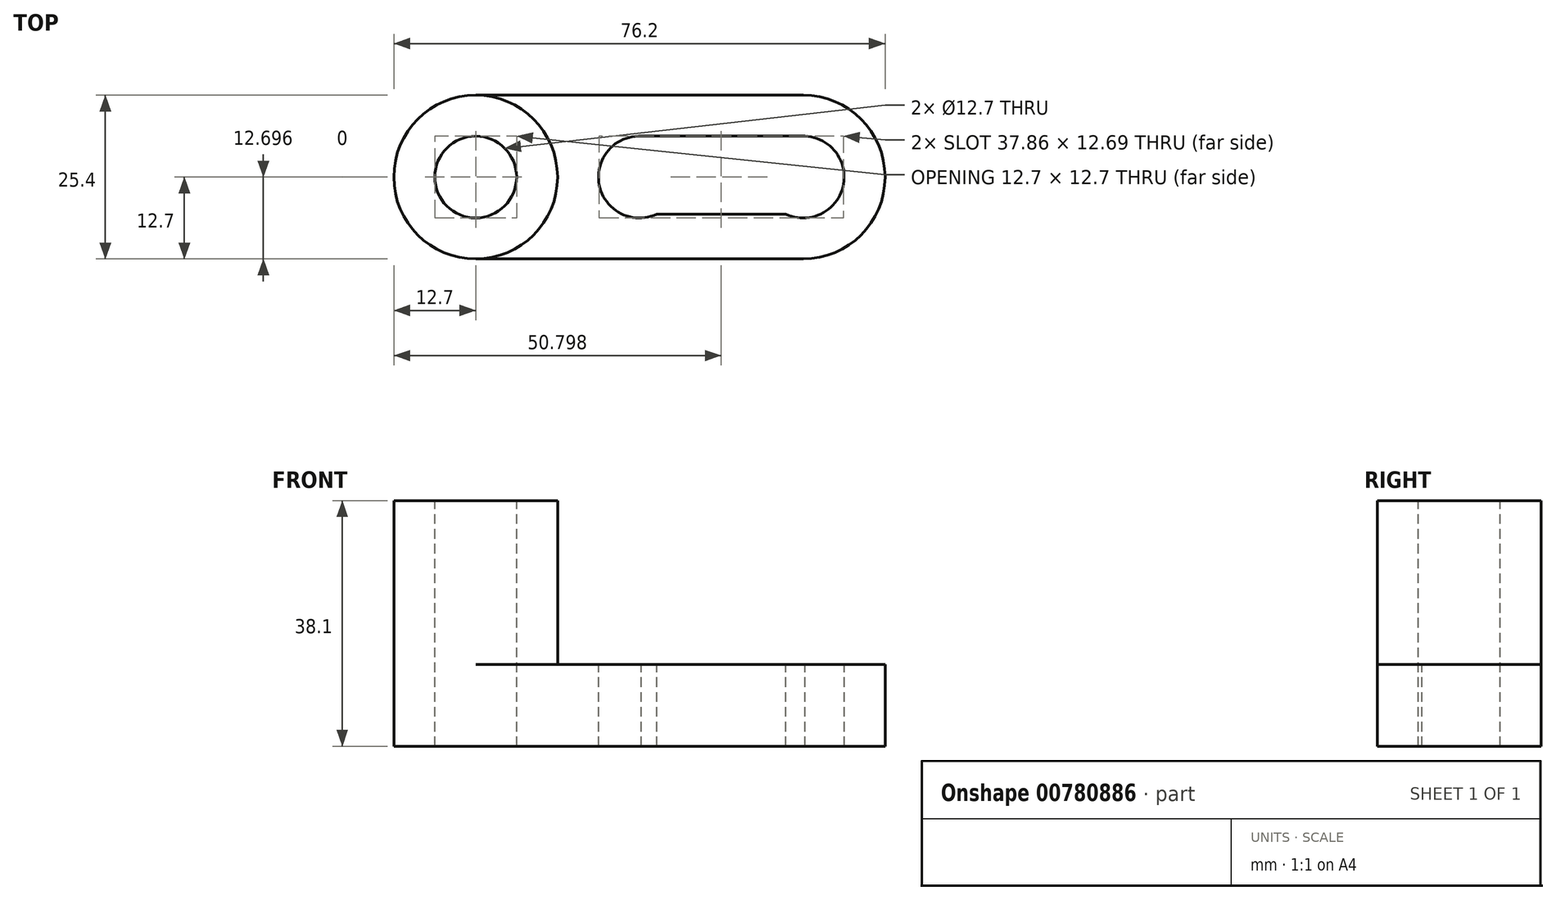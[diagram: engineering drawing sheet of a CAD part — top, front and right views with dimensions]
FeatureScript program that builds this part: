
annotation { "Feature Type Name" : "Feature", "Feature Type Description" : "" }
export const myFeature = defineFeature(function(context is Context, id is Id, definition is map)
    precondition{}
    {
        {
            var Q0;
            Q0=qCreatedBy(makeId("Front.planeOp"),FACE);
            var sketch = newSketch(context, id + "F0", { "sketchPlane" : qUnion([Q0])});
            skLineSegment(sketch, "E0", {"start": v(0, 0) * mm, "end": v(0, 38.1) * mm});
            skLineSegment(sketch, "E1", {"start": v(0, 38.1) * mm, "end": v(25.4, 38.1) * mm});
            skLineSegment(sketch, "E2", {"start": v(25.4, 38.1) * mm, "end": v(25.4, 12.7) * mm});
            skLineSegment(sketch, "E3", {"start": v(25.4, 12.7) * mm, "end": v(76.2, 12.7) * mm});
            skLineSegment(sketch, "E4", {"start": v(76.2, 12.7) * mm, "end": v(76.2, 0) * mm});
            skLineSegment(sketch, "E5", {"start": v(76.2, 0) * mm, "end": v(0, 0) * mm});
            skSolve(sketch);
        }
        {
            var Q0;
            Q0 = qSketchRegion(id + "F0", true);
            extrude(context, id + "F1", {"entities" : qUnion([Q0]), "depth" : 25.4 * mm, "offsetDistance" : 25.4 * mm});
        }
        {
            var Q0;
            Q0=makeQuery(id+"F1.opExtrude","CAP_EDGE",EDGE,{"disambiguationData":[OSD([sQuery(id+"F0.wireOp",EDGE,"E2")])],"isStart":true});
            var Q1;
            Q1=makeQuery(id+"F1.opExtrude","CAP_EDGE",EDGE,{"disambiguationData":[OSD([sQuery(id+"F0.wireOp",EDGE,"E2")])],"isStart":false});
            var Q2;
            Q2=makeQuery(id+"F1.opExtrude","CAP_EDGE",EDGE,{"disambiguationData":[OSD([sQuery(id+"F0.wireOp",EDGE,"E0")])],"isStart":false});
            var Q3;
            Q3=makeQuery(id+"F1.opExtrude","CAP_EDGE",EDGE,{"disambiguationData":[OSD([sQuery(id+"F0.wireOp",EDGE,"E0")])],"isStart":true});
            fillet(context, id + "F2", {"entities" : qUnion([Q0, Q1, Q2, Q3]), "radius" : 12.7 * mm, "tangentPropagation" : true, "allowEdgeOverflow" : false});
        }
        {
            var Q0;
            Q0=makeQuery(id+"F1.opExtrude","SWEPT_FACE",FACE,{"disambiguationData":[OSD([sQuery(id+"F0.wireOp",EDGE,"E1")])]});
            var sketch = newSketch(context, id + "F3", { "sketchPlane" : qUnion([Q0])});
            skCircle(sketch, "E6", {"center": v(12.7, -12.7) * mm, "radius": 6.35 * mm});
            skSolve(sketch);
        }
        {
            var Q0;
            Q0=makeQuery(id+"F3.imprint","IMPRINT",FACE,{"disambiguationData":[TD([[makeQuery(id+"F3.imprint","IMPRINT",EDGE,{"derivedFrom":sQuery(id+"F3.wireOp",EDGE,"E6")}),1.0]])]});
            extrude(context, id + "F4", {"entities" : qUnion([Q0]), "operationType" : NewBodyOperationType.REMOVE, "oppositeDirection" : true, "depth" : 50.8 * mm, "offsetDistance" : 25.4 * mm});
        }
        {
            var Q0;
            Q0=makeQuery(id+"F1.opExtrude","CAP_EDGE",EDGE,{"disambiguationData":[OSD([sQuery(id+"F0.wireOp",EDGE,"E4")])],"isStart":true});
            var Q1;
            Q1=makeQuery(id+"F1.opExtrude","CAP_EDGE",EDGE,{"disambiguationData":[OSD([sQuery(id+"F0.wireOp",EDGE,"E4")])],"isStart":false});
            fillet(context, id + "F5", {"entities" : qUnion([Q0, Q1]), "radius" : 12.7 * mm, "tangentPropagation" : true, "allowEdgeOverflow" : false});
        }
        {
            var Q0;
            Q0=makeQuery(id+"F1.opExtrude","SWEPT_FACE",FACE,{"disambiguationData":[OSD([sQuery(id+"F0.wireOp",EDGE,"E3")])]});
            var sketch = newSketch(context, id + "F6", { "sketchPlane" : qUnion([Q0])});
            skCircle(sketch, "E7", {"center": v(63.5, -12.7) * mm, "radius": 6.35 * mm});
            skCircle(sketch, "E8", {"center": v(38.1, -12.7) * mm, "radius": 6.35 * mm});
            skSolve(sketch);
        }
        {
            var Q0;
            Q0=makeQuery(id+"F6.imprint","IMPRINT",FACE,{"disambiguationData":[TD([[makeQuery(id+"F6.imprint","IMPRINT",EDGE,{"derivedFrom":sQuery(id+"F6.wireOp",EDGE,"E7")}),-1.0]])]});
            var sketch = newSketch(context, id + "F7", { "sketchPlane" : qUnion([Q0])});
            skLineSegment(sketch, "E9", {"start": v(63.73, -18.45) * mm, "end": v(36.13, -18.45) * mm});
            skLineSegment(sketch, "E10", {"start": v(38.3, -6.36) * mm, "end": v(64.04, -6.36) * mm});
            skSolve(sketch);
        }
        {
            var Q0;
            Q0 = qSketchRegion(id + "F7", true);
            var Q1;
            Q1=makeQuery(id+"F6.imprint","IMPRINT",FACE,{"disambiguationData":[TD([[makeQuery(id+"F6.imprint","IMPRINT",EDGE,{"derivedFrom":sQuery(id+"F6.wireOp",EDGE,"E8")}),1.0]])]});
            var Q2;
            {var subQ0=sQuery(id+"F7.wireOp",EDGE,"E9");var subQ1=makeQuery(id+"F6.imprint","IMPRINT",EDGE,{"derivedFrom":sQuery(id+"F6.wireOp",EDGE,"E8")});var subQ2=makeQuery(id+"F7.imprint","INTERSECT",VERTEX,{"derivedFrom":[subQ1,subQ0]});Q2=makeQuery(id+"F7.imprint","IMPRINT",FACE,{"disambiguationData":[TD([[makeQuery(id+"F7.imprint","IMPRINT",EDGE,{"disambiguationData":[TD([[subQ2,1.0]])],"derivedFrom":subQ0}),-1.0]])]});}
            var Q3;
            {var subQ0=sQuery(id+"F7.wireOp",EDGE,"E10");var subQ1=makeQuery(id+"F6.imprint","IMPRINT",EDGE,{"derivedFrom":sQuery(id+"F6.wireOp",EDGE,"E7")});var subQ2=makeQuery(id+"F7.imprint","INTERSECT",VERTEX,{"disambiguationData":[OD(0.0)],"derivedFrom":[subQ1,subQ0]});Q3=makeQuery(id+"F7.imprint","IMPRINT",FACE,{"disambiguationData":[TD([[makeQuery(id+"F7.imprint","IMPRINT",EDGE,{"disambiguationData":[TD([[subQ2,1.0]])],"derivedFrom":subQ0}),-1.0]])]});}
            extrude(context, id + "F8", {"entities" : qUnion([Q0, Q1, Q2, Q3]), "operationType" : NewBodyOperationType.REMOVE, "oppositeDirection" : true, "depth" : 25.4 * mm, "offsetDistance" : 25.4 * mm});
        }
    });
